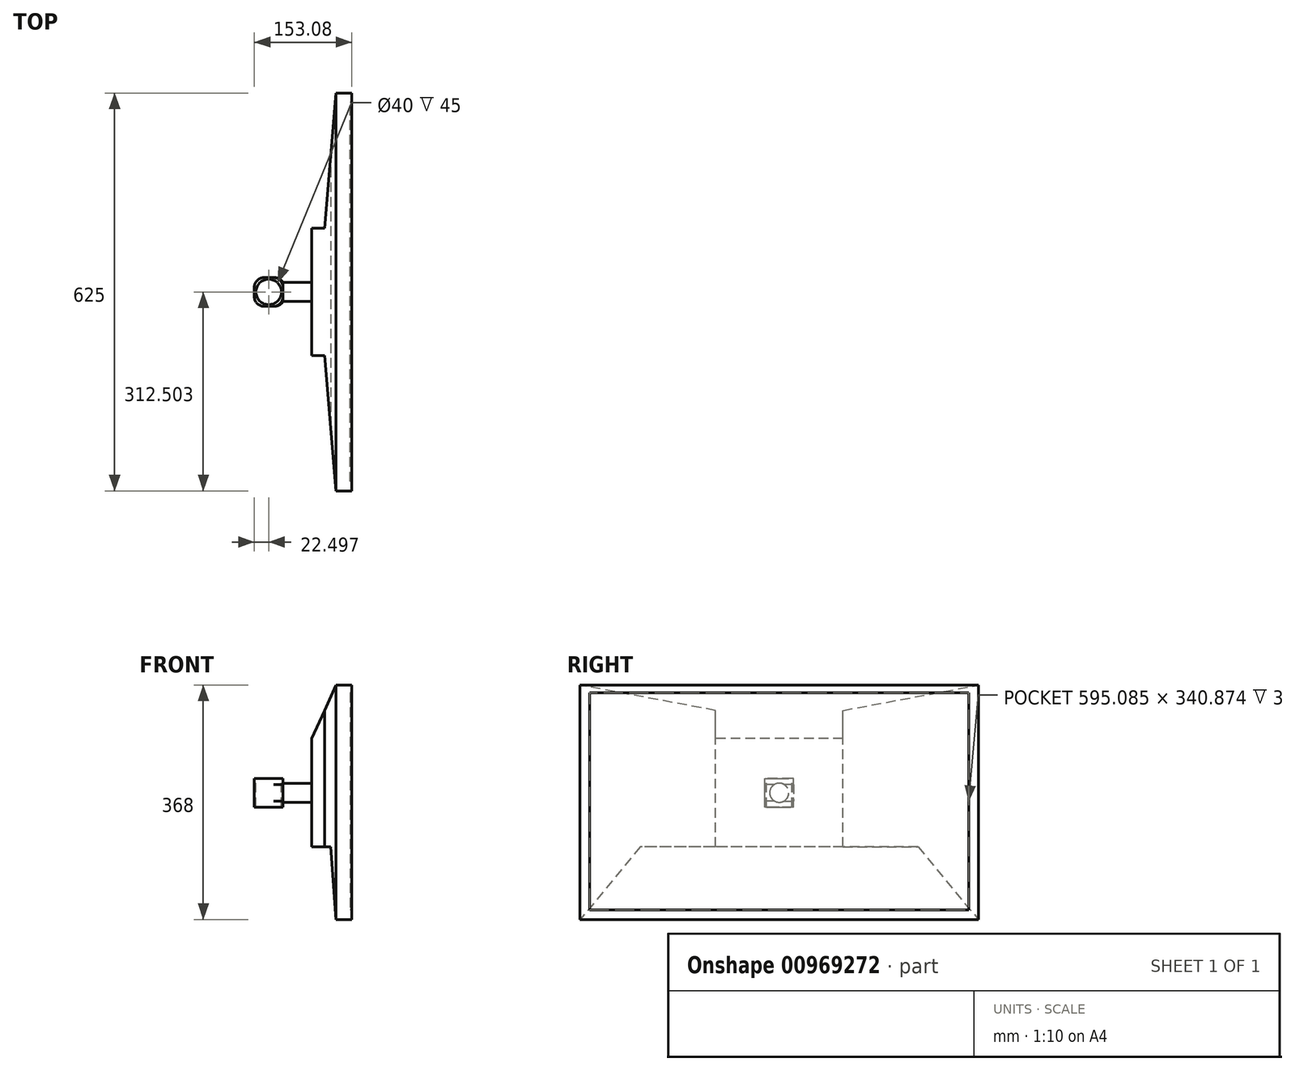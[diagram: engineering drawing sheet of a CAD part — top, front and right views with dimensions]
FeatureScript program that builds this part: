
annotation { "Feature Type Name" : "Feature", "Feature Type Description" : "" }
export const myFeature = defineFeature(function(context is Context, id is Id, definition is map)
    precondition{}
    {
        {
            var Q0;
            Q0=qCreatedBy(makeId("Right.planeOp"),FACE);
            var sketch = newSketch(context, id + "F0", { "sketchPlane" : qUnion([Q0])});
            skLineSegment(sketch, "E0.bottom", {"start": v(-306.7, 206.58) * mm, "end": v(318.3, 206.58) * mm});
            skLineSegment(sketch, "E0.top", {"start": v(-306.7, -161.42) * mm, "end": v(318.3, -161.42) * mm});
            skLineSegment(sketch, "E0.left", {"start": v(-306.7, 206.58) * mm, "end": v(-306.7, -161.42) * mm});
            skLineSegment(sketch, "E0.right", {"start": v(318.3, 206.58) * mm, "end": v(318.3, -161.42) * mm});
            skLineSegment(sketch, "E1.bottom", {"start": v(-291.74, 194.41) * mm, "end": v(303.35, 194.41) * mm});
            skLineSegment(sketch, "E1.top", {"start": v(-291.74, -146.46) * mm, "end": v(303.35, -146.46) * mm});
            skLineSegment(sketch, "E1.left", {"start": v(-291.74, 194.41) * mm, "end": v(-291.74, -146.46) * mm});
            skLineSegment(sketch, "E1.right", {"start": v(303.35, 194.41) * mm, "end": v(303.35, -146.46) * mm});
            skLineSegment(sketch, "E2", {"start": v(-291.74, 194.41) * mm, "end": v(303.35, -146.46) * mm, "construction": true});
            skLineSegment(sketch, "E3", {"start": v(-306.7, 206.58) * mm, "end": v(318.3, -161.42) * mm, "construction": true});
            skPoint(sketch, "E4", {"position": v(5.8, 22.58) * mm});
            skPoint(sketch, "E5", {"position": v(5.8, 23.98) * mm});
            skSolve(sketch);
        }
        {
            var Q0;
            Q0=makeQuery(id+"F0.imprint","IMPRINT",FACE,{"disambiguationData":[TD([[makeQuery(id+"F0.imprint","IMPRINT",EDGE,{"derivedFrom":sQuery(id+"F0.wireOp",EDGE,"E1.bottom")}),-1.0]])]});
            var sketch = newSketch(context, id + "F1", { "sketchPlane" : qUnion([Q0])});
            skSolve(sketch);
        }
        {
            var Q0;
            Q0=makeQuery(id+"F0.imprint","IMPRINT",FACE,{"disambiguationData":[TD([[makeQuery(id+"F0.imprint","IMPRINT",EDGE,{"derivedFrom":sQuery(id+"F0.wireOp",EDGE,"E0.bottom")}),-1.0]])]});
            extrude(context, id + "F2", {"entities" : qUnion([Q0]), "depth" : 25 * mm, "offsetDistance" : 25 * mm});
        }
        {
            var Q0;
            Q0=makeQuery(id+"F1.imprint","IMPRINT",FACE,{"disambiguationData":[TD([[makeQuery(id+"F1.imprint","IMPRINT",EDGE,{"derivedFrom":makeQuery(id+"F0.imprint","IMPRINT",EDGE,{"derivedFrom":sQuery(id+"F0.wireOp",EDGE,"E1.bottom")})}),-1.0]])]});
            extrude(context, id + "F3", {"entities" : qUnion([Q0]), "operationType" : NewBodyOperationType.ADD, "depth" : 22 * mm, "offsetDistance" : 25 * mm});
        }
        {
            var Q0;
            Q0=makeQuery(id+"F2.opExtrude","SWEPT_FACE",FACE,{"disambiguationData":[OSD([sQuery(id+"F0.wireOp",EDGE,"E0.bottom")])]});
            var sketch = newSketch(context, id + "F4", { "sketchPlane" : qUnion([Q0])});
            skLineSegment(sketch, "E6.bottom", {"start": v(25, 318.3) * mm, "end": v(0, 318.3) * mm, "construction": true});
            skLineSegment(sketch, "E6.top", {"start": v(25, -306.7) * mm, "end": v(0, -306.7) * mm, "construction": true});
            skLineSegment(sketch, "E6.left", {"start": v(25, 318.3) * mm, "end": v(25, -306.7) * mm, "construction": true});
            skLineSegment(sketch, "E6.right", {"start": v(0, 318.3) * mm, "end": v(0, -306.7) * mm});
            skLineSegment(sketch, "E7", {"start": v(25, 5.8) * mm, "end": v(-38, 5.8) * mm, "construction": true});
            skLineSegment(sketch, "E8", {"start": v(-38, 5.8) * mm, "end": v(-38, 105.8) * mm});
            skLineSegment(sketch, "E9", {"start": v(-38, 105.8) * mm, "end": v(-18, 105.8) * mm});
            skLineSegment(sketch, "E10", {"start": v(-38, 5.8) * mm, "end": v(-38, -94.2) * mm});
            skLineSegment(sketch, "E11", {"start": v(-38, -94.2) * mm, "end": v(-18, -94.2) * mm});
            skLineSegment(sketch, "E12", {"start": v(-18, 105.8) * mm, "end": v(0, 318.3) * mm});
            skLineSegment(sketch, "E13", {"start": v(-18, -94.2) * mm, "end": v(0, -306.7) * mm});
            skSolve(sketch);
        }
        {
            var Q0;
            Q0=makeQuery(id+"F4.imprint","IMPRINT",FACE,{"disambiguationData":[TD([[makeQuery(id+"F4.imprint","IMPRINT",EDGE,{"derivedFrom":sQuery(id+"F4.wireOp",EDGE,"E6.right")}),1.0]])]});
            var Q1;
            Q1=makeQuery(id+"F2.opExtrude","SWEPT_FACE",FACE,{"disambiguationData":[OSD([sQuery(id+"F0.wireOp",EDGE,"E0.top")])]});
            extrude(context, id + "F5", {"entities" : qUnion([Q0]), "operationType" : NewBodyOperationType.ADD, "endBound" : BoundingType.UP_TO_SURFACE, "oppositeDirection" : true, "depth" : 25 * mm, "endBoundEntityFace" : qUnion([Q1]), "offsetDistance" : 25 * mm});
        }
        {
            var Q0;
            Q0=makeQuery(id+"F2.opExtrude","SWEPT_FACE",FACE,{"disambiguationData":[OSD([sQuery(id+"F0.wireOp",EDGE,"E0.left")])]});
            var sketch = newSketch(context, id + "F6", { "sketchPlane" : qUnion([Q0])});
            skLineSegment(sketch, "E14.bottom", {"start": v(25, 206.58) * mm, "end": v(0, 206.58) * mm, "construction": true});
            skLineSegment(sketch, "E14.top", {"start": v(25, -161.42) * mm, "end": v(0, -161.42) * mm, "construction": true});
            skLineSegment(sketch, "E14.left", {"start": v(25, 206.58) * mm, "end": v(25, -161.42) * mm, "construction": true});
            skLineSegment(sketch, "E14.right", {"start": v(0, 206.58) * mm, "end": v(0, -161.42) * mm, "construction": true});
            skLineSegment(sketch, "E15", {"start": v(25, 22.58) * mm, "end": v(-38, 22.58) * mm, "construction": true});
            skLineSegment(sketch, "E16", {"start": v(-38, 22.58) * mm, "end": v(-38, 122.58) * mm, "construction": true});
            skLineSegment(sketch, "E17", {"start": v(-38, 122.58) * mm, "end": v(-38, 122.58) * mm});
            skLineSegment(sketch, "E18", {"start": v(-38, 22.58) * mm, "end": v(-38, -47.42) * mm, "construction": true});
            skLineSegment(sketch, "E19", {"start": v(-38, -47.42) * mm, "end": v(-8, -47.42) * mm});
            skLineSegment(sketch, "E20", {"start": v(-8, -47.42) * mm, "end": v(0, -161.42) * mm});
            skLineSegment(sketch, "E21", {"start": v(0, -161.42) * mm, "end": v(-38, -161.42) * mm});
            skLineSegment(sketch, "E22", {"start": v(-38, -47.42) * mm, "end": v(-38, -161.42) * mm});
            skLineSegment(sketch, "E23", {"start": v(-38, 122.58) * mm, "end": v(-38, 206.58) * mm});
            skLineSegment(sketch, "E24", {"start": v(0, 206.58) * mm, "end": v(-38, 206.58) * mm});
            skLineSegment(sketch, "E25", {"start": v(-38, 122.58) * mm, "end": v(0, 206.58) * mm});
            skSolve(sketch);
        }
        {
            var Q0;
            Q0=makeQuery(id+"F6.imprint","IMPRINT",FACE,{"disambiguationData":[TD([[makeQuery(id+"F6.imprint","IMPRINT",EDGE,{"derivedFrom":sQuery(id+"F6.wireOp",EDGE,"E19")}),-1.0]])]});
            var Q1;
            Q1=makeQuery(id+"F2.opExtrude","SWEPT_FACE",FACE,{"disambiguationData":[OSD([sQuery(id+"F0.wireOp",EDGE,"E0.right")])]});
            extrude(context, id + "F7", {"entities" : qUnion([Q0]), "operationType" : NewBodyOperationType.REMOVE, "endBound" : BoundingType.UP_TO_SURFACE, "oppositeDirection" : true, "depth" : 25 * mm, "endBoundEntityFace" : qUnion([Q1]), "offsetDistance" : 25 * mm});
        }
        {
            var Q0;
            Q0=makeQuery(id+"F6.imprint","IMPRINT",FACE,{"disambiguationData":[TD([[makeQuery(id+"F6.imprint","IMPRINT",EDGE,{"derivedFrom":sQuery(id+"F6.wireOp",EDGE,"E23")}),-1.0]])]});
            var Q1;
            Q1=makeQuery(id+"F2.opExtrude","SWEPT_FACE",FACE,{"disambiguationData":[OSD([sQuery(id+"F0.wireOp",EDGE,"E0.right")])]});
            extrude(context, id + "F8", {"entities" : qUnion([Q0]), "operationType" : NewBodyOperationType.REMOVE, "endBound" : BoundingType.UP_TO_SURFACE, "oppositeDirection" : true, "depth" : 25 * mm, "endBoundEntityFace" : qUnion([Q1]), "offsetDistance" : 25 * mm});
        }
        {
            var Q0;
            Q0=makeQuery(id+"F5.opExtrude","SWEPT_FACE",FACE,{"disambiguationData":[OSD([sQuery(id+"F4.wireOp",EDGE,"E8"),sQuery(id+"F4.wireOp",EDGE,"E10")])]});
            var sketch = newSketch(context, id + "F9", { "sketchPlane" : qUnion([Q0])});
            skLineSegment(sketch, "E26", {"start": v(-105.8, 122.58) * mm, "end": v(94.2, -47.42) * mm, "construction": true});
            skLineSegment(sketch, "E27", {"start": v(94.2, 122.58) * mm, "end": v(-105.8, -47.42) * mm, "construction": true});
            skCircle(sketch, "E28", {"center": v(-5.8, 37.58) * mm, "radius": 15 * mm});
            skSolve(sketch);
        }
        {
            var Q0;
            Q0=makeQuery(id+"F9.imprint","IMPRINT",FACE,{"disambiguationData":[TD([[makeQuery(id+"F9.imprint","IMPRINT",EDGE,{"derivedFrom":sQuery(id+"F9.wireOp",EDGE,"E28")}),1.0]])]});
            extrude(context, id + "F10", {"entities" : qUnion([Q0]), "operationType" : NewBodyOperationType.ADD, "depth" : 45.08 * mm, "offsetDistance" : 25 * mm});
        }
        {
            var Q0;
            Q0=makeQuery(id+"F10.opExtrude","CAP_FACE",FACE,{"disambiguationData":[OSD([sQuery(id+"F9.wireOp",EDGE,"E28")])],"isStart":false});
            var sketch = newSketch(context, id + "F11", { "sketchPlane" : qUnion([Q0])});
            skCircle(sketch, "E29.0", {"center": v(-5.8, 37.58) * mm, "radius": 15 * mm, "construction": true});
            skLineSegment(sketch, "E30.bottom", {"start": v(16.7, 15.08) * mm, "end": v(-28.3, 15.08) * mm});
            skLineSegment(sketch, "E30.top", {"start": v(16.7, 60.08) * mm, "end": v(-28.3, 60.08) * mm});
            skLineSegment(sketch, "E30.left", {"start": v(16.7, 15.08) * mm, "end": v(16.7, 60.08) * mm});
            skLineSegment(sketch, "E30.right", {"start": v(-28.3, 15.08) * mm, "end": v(-28.3, 60.08) * mm});
            skSolve(sketch);
        }
        {
            var Q0;
            Q0=makeQuery(id+"F11.imprint","IMPRINT",FACE,{"disambiguationData":[TD([[makeQuery(id+"F11.imprint","IMPRINT",EDGE,{"derivedFrom":sQuery(id+"F11.wireOp",EDGE,"E30.bottom")}),-1.0]])]});
            var Q1;
            Q1=makeQuery(id+"F11.imprint","IMPRINT",FACE,{"disambiguationData":[TD([[makeQuery(id+"F11.imprint","IMPRINT",EDGE,{"derivedFrom":makeQuery(id+"F10.opExtrude","CAP_EDGE",EDGE,{"disambiguationData":[OSD([sQuery(id+"F9.wireOp",EDGE,"E28")])],"isStart":false})}),1.0]])]});
            extrude(context, id + "F12", {"entities" : qUnion([Q0, Q1]), "operationType" : NewBodyOperationType.ADD, "depth" : 45 * mm, "offsetDistance" : 25 * mm});
        }
        {
            var Q0;
            Q0=makeQuery(id+"F12.opExtrude","SWEPT_FACE",FACE,{"disambiguationData":[OSD([sQuery(id+"F11.wireOp",EDGE,"E30.top")])]});
            var sketch = newSketch(context, id + "F13", { "sketchPlane" : qUnion([Q0])});
            skLineSegment(sketch, "E31", {"start": v(-83.08, -16.7) * mm, "end": v(-128.08, 28.3) * mm, "construction": true});
            skLineSegment(sketch, "E32", {"start": v(-128.08, -16.7) * mm, "end": v(-83.08, 28.3) * mm, "construction": true});
            skCircle(sketch, "E33", {"center": v(-105.58, 5.8) * mm, "radius": 20 * mm});
            skSolve(sketch);
        }
        {
            var Q0;
            Q0=makeQuery(id+"F13.imprint","IMPRINT",FACE,{"disambiguationData":[TD([[makeQuery(id+"F13.imprint","IMPRINT",EDGE,{"derivedFrom":sQuery(id+"F13.wireOp",EDGE,"E33")}),1.0]])]});
            extrude(context, id + "F14", {"entities" : qUnion([Q0]), "operationType" : NewBodyOperationType.REMOVE, "endBound" : BoundingType.UP_TO_NEXT, "oppositeDirection" : true, "depth" : 25 * mm, "offsetDistance" : 25 * mm});
        }
        {
            var Q0;
            Q0=makeQuery(id+"F12.opExtrude","CAP_EDGE",EDGE,{"disambiguationData":[OSD([sQuery(id+"F11.wireOp",EDGE,"E30.left")])],"isStart":true});
            var Q1;
            Q1=makeQuery(id+"F12.opExtrude","CAP_EDGE",EDGE,{"disambiguationData":[OSD([sQuery(id+"F11.wireOp",EDGE,"E30.left")])],"isStart":false});
            var Q2;
            Q2=makeQuery(id+"F12.opExtrude","CAP_EDGE",EDGE,{"disambiguationData":[OSD([sQuery(id+"F11.wireOp",EDGE,"E30.right")])],"isStart":false});
            var Q3;
            Q3=makeQuery(id+"F12.opExtrude","CAP_EDGE",EDGE,{"disambiguationData":[OSD([sQuery(id+"F11.wireOp",EDGE,"E30.right")])],"isStart":true});
            fillet(context, id + "F15", {"entities" : qUnion([Q0, Q1, Q2, Q3]), "radius" : 15 * mm, "tangentPropagation" : true, "allowEdgeOverflow" : false});
        }
    });
